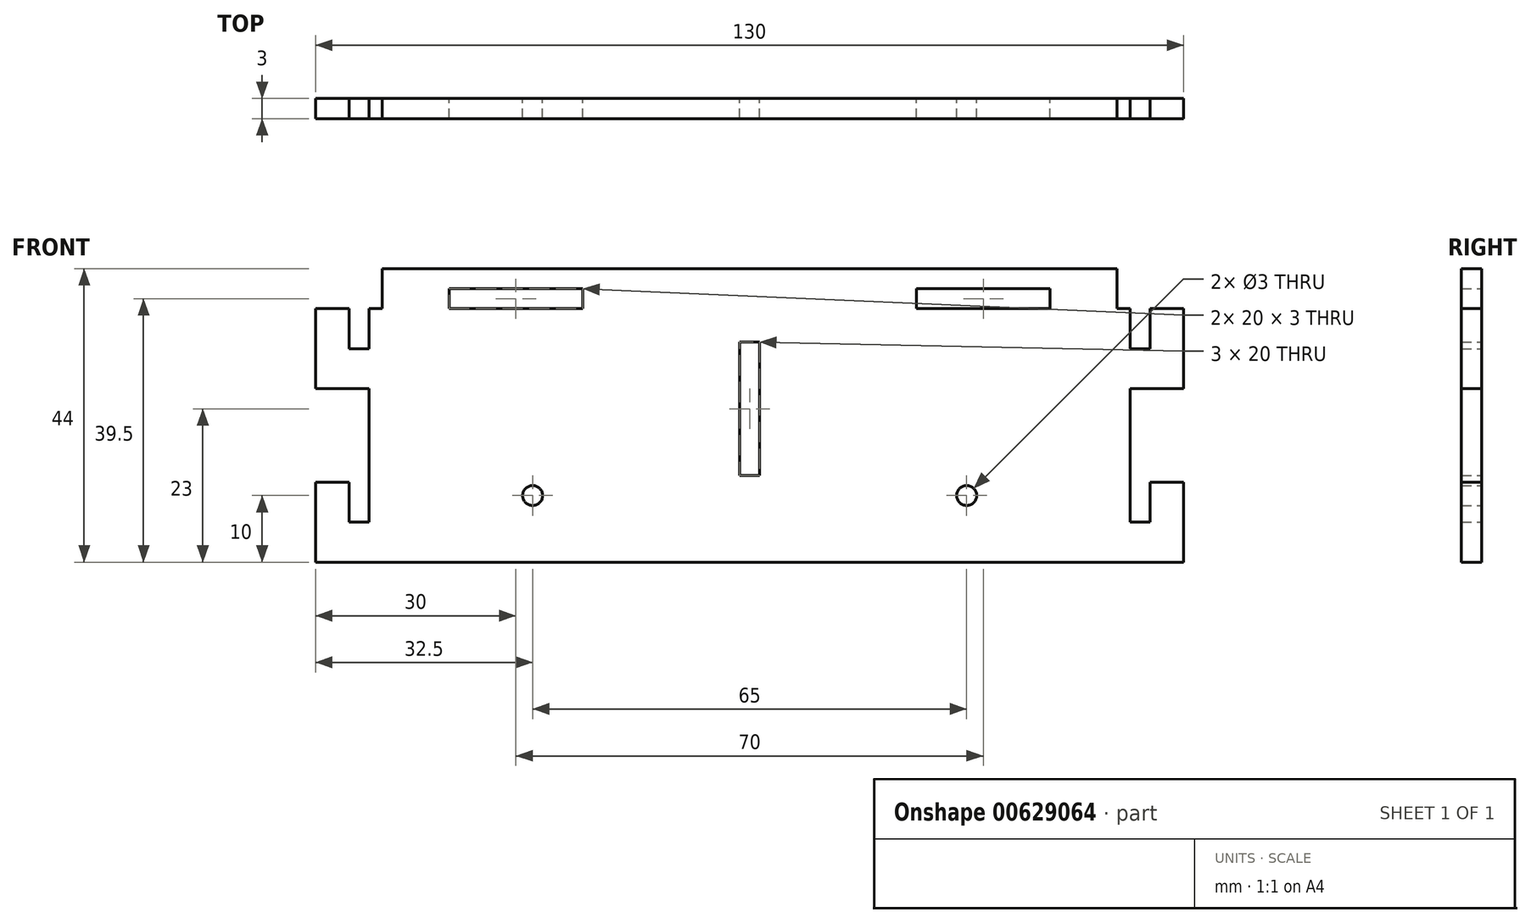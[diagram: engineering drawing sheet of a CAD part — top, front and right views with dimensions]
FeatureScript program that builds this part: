
annotation { "Feature Type Name" : "Feature", "Feature Type Description" : "" }
export const myFeature = defineFeature(function(context is Context, id is Id, definition is map)
    precondition{}
    {
        {
            var Q0;
            Q0=qCreatedBy(makeId("Front.planeOp"),FACE);
            var sketch = newSketch(context, id + "F0", { "sketchPlane" : qUnion([Q0])});
            skLineSegment(sketch, "E0.bottom", {"start": v(-55, 34) * mm, "end": v(55, 34) * mm});
            skLineSegment(sketch, "E0.top", {"start": v(-65, -10) * mm, "end": v(65, -10) * mm});
            skLineSegment(sketch, "E0.right", {"start": v(65, 28) * mm, "end": v(65, 16) * mm});
            skLineSegment(sketch, "E1.bottom", {"start": v(-45, 31) * mm, "end": v(-25, 31) * mm});
            skLineSegment(sketch, "E1.top", {"start": v(-45, 28) * mm, "end": v(-25, 28) * mm});
            skLineSegment(sketch, "E1.left", {"start": v(-45, 31) * mm, "end": v(-45, 28) * mm});
            skLineSegment(sketch, "E1.right", {"start": v(-25, 31) * mm, "end": v(-25, 28) * mm});
            skLineSegment(sketch, "E2.right", {"start": v(-55, 28) * mm, "end": v(-55, 34) * mm});
            skLineSegment(sketch, "E3", {"start": v(0, 47.65) * mm, "end": v(0, -51.42) * mm, "construction": true});
            skPoint(sketch, "E3.endSnap0", {"position": v(0, -10) * mm});
            skLineSegment(sketch, "E4.trimOffspring", {"start": v(-57, 28) * mm, "end": v(-55, 28) * mm});
            skLineSegment(sketch, "E5", {"start": v(-79.24, 0) * mm, "end": v(85.77, 0) * mm, "construction": true});
            skCircle(sketch, "E6", {"center": v(-32.5, 0) * mm, "radius": 1.5 * mm});
            skCircle(sketch, "E7", {"center": v(32.5, 0) * mm, "radius": 1.5 * mm});
            skLineSegment(sketch, "E8", {"start": v(-57, 28) * mm, "end": v(-57, 22) * mm});
            skLineSegment(sketch, "E9", {"start": v(-57, 22) * mm, "end": v(-60, 22) * mm});
            skLineSegment(sketch, "E10", {"start": v(-60, 22) * mm, "end": v(-60, 28) * mm});
            skLineSegment(sketch, "E11", {"start": v(-65, 28) * mm, "end": v(-65, 22) * mm});
            skLineSegment(sketch, "E12", {"start": v(-65, 16) * mm, "end": v(-57, 16) * mm});
            skLineSegment(sketch, "E13", {"start": v(-57, 16) * mm, "end": v(-57, -4) * mm});
            skLineSegment(sketch, "E14", {"start": v(-57, -4) * mm, "end": v(-60, -4) * mm});
            skLineSegment(sketch, "E15", {"start": v(-60, -4) * mm, "end": v(-60, 2) * mm});
            skLineSegment(sketch, "E16", {"start": v(-65, 2) * mm, "end": v(-65, -4) * mm});
            skLineSegment(sketch, "E17", {"start": v(-65, 22) * mm, "end": v(-65, 16) * mm});
            skLineSegment(sketch, "E18", {"start": v(-65, -4) * mm, "end": v(-65, -10) * mm});
            skLineSegment(sketch, "E19.MirrorCS", {"start": v(60, 22) * mm, "end": v(60, 28) * mm});
            skLineSegment(sketch, "E20.MirrorCS", {"start": v(57, -4) * mm, "end": v(60, -4) * mm});
            skLineSegment(sketch, "E21.MirrorCS", {"start": v(65, -4) * mm, "end": v(65, -10) * mm});
            skLineSegment(sketch, "E22.MirrorCS", {"start": v(65, 28) * mm, "end": v(60, 28) * mm});
            skLineSegment(sketch, "E23.MirrorCS", {"start": v(60, 2) * mm, "end": v(65, 2) * mm});
            skLineSegment(sketch, "E24.MirrorCS", {"start": v(65, 2) * mm, "end": v(65, -4) * mm});
            skLineSegment(sketch, "E25.MirrorCS", {"start": v(57, 16) * mm, "end": v(57, -4) * mm});
            skLineSegment(sketch, "E26.MirrorCS", {"start": v(57, 22) * mm, "end": v(60, 22) * mm});
            skLineSegment(sketch, "E27.MirrorCS", {"start": v(57, 28) * mm, "end": v(57, 22) * mm});
            skLineSegment(sketch, "E28.MirrorCS", {"start": v(65, 16) * mm, "end": v(57, 16) * mm});
            skLineSegment(sketch, "E29.MirrorCS", {"start": v(65, 28) * mm, "end": v(65, 22) * mm});
            skLineSegment(sketch, "E30.MirrorCS", {"start": v(60, -4) * mm, "end": v(60, 2) * mm});
            skLineSegment(sketch, "E31.MirrorCS", {"start": v(65, 22) * mm, "end": v(65, 16) * mm});
            skLineSegment(sketch, "E32.MirrorCS", {"start": v(45, 31) * mm, "end": v(45, 28) * mm});
            skLineSegment(sketch, "E33.MirrorCS", {"start": v(45, 28) * mm, "end": v(25, 28) * mm});
            skLineSegment(sketch, "E34.MirrorCS", {"start": v(45, 31) * mm, "end": v(25, 31) * mm});
            skLineSegment(sketch, "E35.MirrorCS", {"start": v(25, 31) * mm, "end": v(25, 28) * mm});
            skLineSegment(sketch, "E36.MirrorCS", {"start": v(57, 28) * mm, "end": v(55, 28) * mm});
            skLineSegment(sketch, "E37.MirrorCS", {"start": v(55, 28) * mm, "end": v(55, 34) * mm});
            skLineSegment(sketch, "E38.trimOffspring", {"start": v(65, 2) * mm, "end": v(65, -10) * mm});
            skLineSegment(sketch, "E39.bottom", {"start": v(-1.5, 23) * mm, "end": v(1.5, 23) * mm});
            skLineSegment(sketch, "E39.top", {"start": v(-1.5, 3) * mm, "end": v(1.5, 3) * mm});
            skLineSegment(sketch, "E39.left", {"start": v(-1.5, 23) * mm, "end": v(-1.5, 3) * mm});
            skLineSegment(sketch, "E39.right", {"start": v(1.5, 23) * mm, "end": v(1.5, 3) * mm});
            skLineSegment(sketch, "E40", {"start": v(-60, 28) * mm, "end": v(-65, 28) * mm});
            skLineSegment(sketch, "E41", {"start": v(-60, 2) * mm, "end": v(-65, 2) * mm});
            skSolve(sketch);
        }
        {
            var Q0;
            Q0=qSketchRegion(id+"F0",true);
            extrude(context, id + "F1", {"entities" : qUnion([Q0]), "endBound" : BoundingType.SYMMETRIC, "depth" : 3 * mm, "offsetDistance" : 25 * mm});
        }
    });
